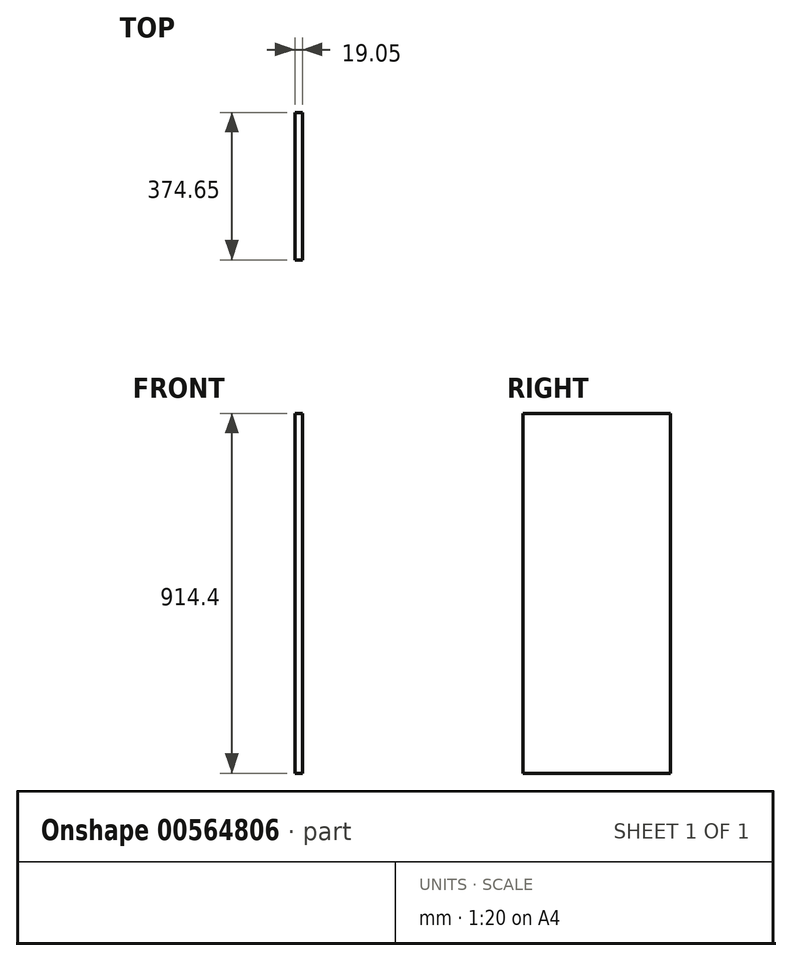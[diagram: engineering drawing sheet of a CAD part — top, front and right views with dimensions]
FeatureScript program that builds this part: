
annotation { "Feature Type Name" : "Feature", "Feature Type Description" : "" }
export const myFeature = defineFeature(function(context is Context, id is Id, definition is map)
    precondition{}
    {
        {
            var Q0;
            Q0=qCreatedBy(makeId("Front.planeOp"),FACE);
            var sketch = newSketch(context, id + "F0", { "sketchPlane" : qUnion([Q0])});
            skLineSegment(sketch, "E0.bottom", {"start": v(-109.18, 501.76) * mm, "end": v(-90.13, 501.76) * mm});
            skLineSegment(sketch, "E0.top", {"start": v(-109.18, -412.64) * mm, "end": v(-90.13, -412.64) * mm});
            skLineSegment(sketch, "E0.left", {"start": v(-109.18, 501.76) * mm, "end": v(-109.18, -412.64) * mm});
            skLineSegment(sketch, "E0.right", {"start": v(-90.13, 501.76) * mm, "end": v(-90.13, -412.64) * mm});
            skSolve(sketch);
        }
        {
            var Q0;
            Q0=makeQuery(id+"F0.imprint","IMPRINT",FACE,{"disambiguationData":[TD([[makeQuery(id+"F0.imprint","IMPRINT",EDGE,{"derivedFrom":sQuery(id+"F0.wireOp",EDGE,"E0.bottom")}),-1.0]])]});
            extrude(context, id + "F1", {"entities" : qUnion([Q0]), "depth" : 374.65 * mm, "offsetDistance" : 25.4 * mm});
        }
    });
